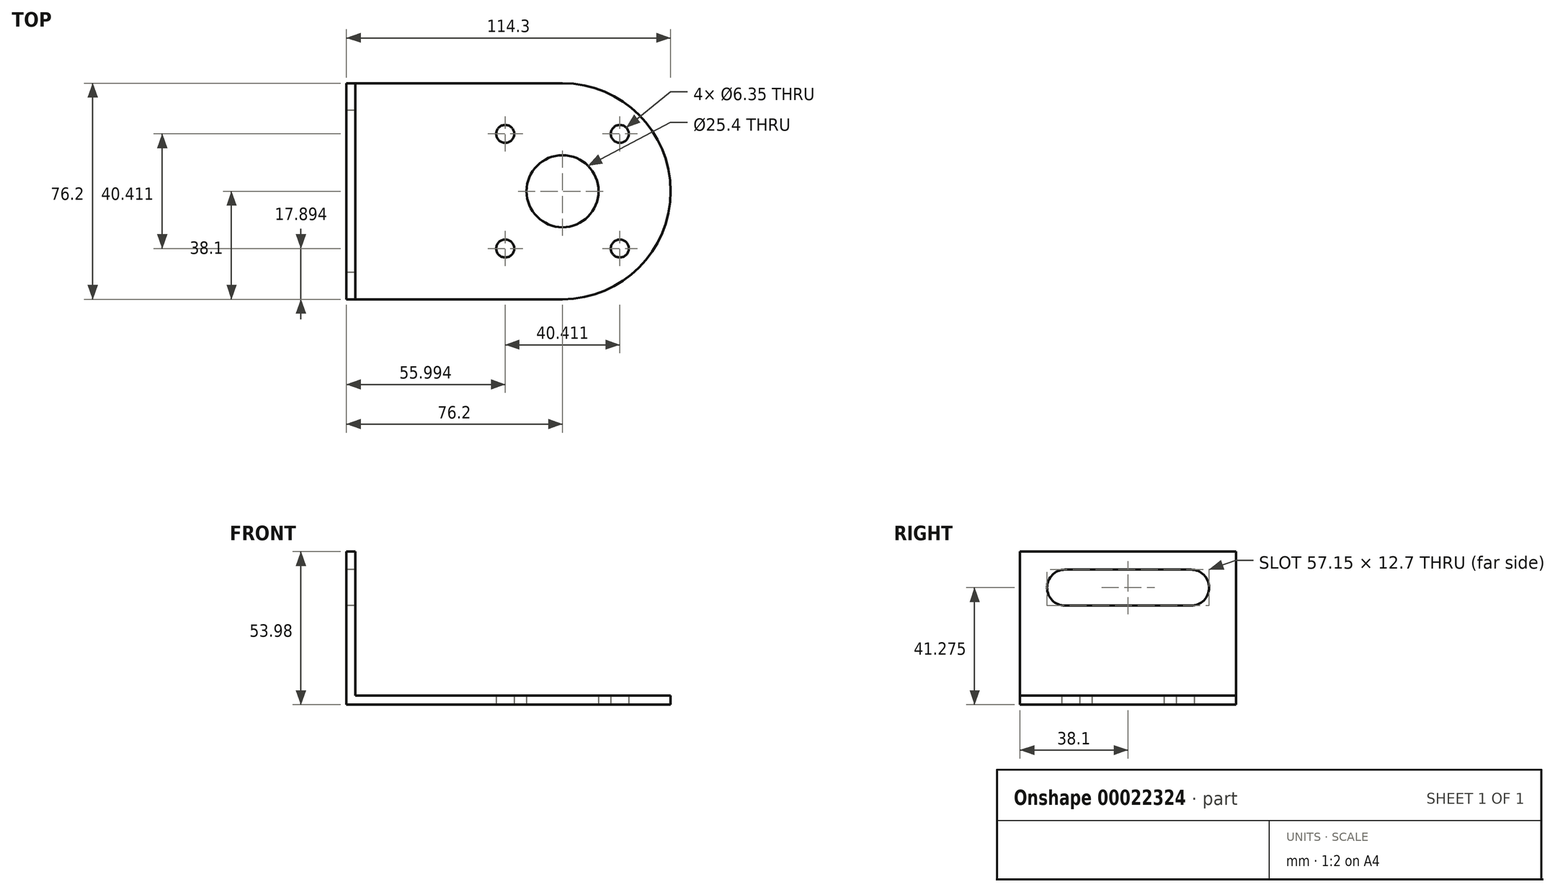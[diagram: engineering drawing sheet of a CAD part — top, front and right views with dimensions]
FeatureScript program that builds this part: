
annotation { "Feature Type Name" : "Feature", "Feature Type Description" : "" }
export const myFeature = defineFeature(function(context is Context, id is Id, definition is map)
    precondition{}
    {
        {
            var Q0;
            Q0=qCreatedBy(makeId("Top.planeOp"),FACE);
            var sketch = newSketch(context, id + "F0", { "sketchPlane" : qUnion([Q0])});
            skLineSegment(sketch, "E0.bottom", {"start": v(0, 76.2) * mm, "end": v(76.2, 76.2) * mm});
            skLineSegment(sketch, "E0.top", {"start": v(0, 0) * mm, "end": v(76.2, 0) * mm});
            skLineSegment(sketch, "E0.left", {"start": v(0, 76.2) * mm, "end": v(0, 0) * mm});
            skArc(sketch, "E1", {"start": v(76.2, 0) * mm, "mid": v(114.3, 38.1) * mm, "end": v(76.2, 76.2) * mm});
            skCircle(sketch, "E2", {"center": v(76.2, 38.1) * mm, "radius": 12.7 * mm});
            skCircle(sketch, "E3", {"center": v(76.2, 38.1) * mm, "radius": 28.58 * mm, "construction": true});
            skLineSegment(sketch, "E4", {"start": v(76.2, 38.1) * mm, "end": v(32.24, 38.1) * mm, "construction": true});
            skLineSegment(sketch, "E5", {"start": v(76.2, 38.1) * mm, "end": v(45.25, 69.05) * mm, "construction": true});
            skCircle(sketch, "E6", {"center": v(56, 58.3) * mm, "radius": 3.18 * mm});
            skCircle(sketch, "E7.1.0", {"center": v(56, 17.9) * mm, "radius": 3.18 * mm});
            skCircle(sketch, "E7.2.0", {"center": v(96.4, 17.9) * mm, "radius": 3.18 * mm});
            skCircle(sketch, "E7.3.0", {"center": v(96.4, 58.3) * mm, "radius": 3.18 * mm});
            skLineSegment(sketch, "E8", {"start": v(76.2, 38.1) * mm, "end": v(114.3, 38.1) * mm, "construction": true});
            skLineSegment(sketch, "E9", {"start": v(32.24, 38.1) * mm, "end": v(0, 38.1) * mm, "construction": true});
            skSolve(sketch);
        }
        {
            var Q0;
            Q0=qCreatedBy(makeId("Right.planeOp"),FACE);
            var sketch = newSketch(context, id + "F1", { "sketchPlane" : qUnion([Q0])});
            skLineSegment(sketch, "E10.bottom", {"start": v(0, 53.98) * mm, "end": v(76.2, 53.98) * mm});
            skLineSegment(sketch, "E10.top", {"start": v(0, 0) * mm, "end": v(76.2, 0) * mm});
            skLineSegment(sketch, "E10.left", {"start": v(0, 53.98) * mm, "end": v(0, 0) * mm});
            skLineSegment(sketch, "E10.right", {"start": v(76.2, 53.98) * mm, "end": v(76.2, 0) * mm});
            skLineSegment(sketch, "E11", {"start": v(0, 41.28) * mm, "end": v(76.2, 41.28) * mm, "construction": true});
            skArc(sketch, "E12", {"start": v(15.88, 47.63) * mm, "mid": v(9.53, 41.28) * mm, "end": v(15.88, 34.93) * mm});
            skArc(sketch, "E13", {"start": v(60.33, 34.93) * mm, "mid": v(66.67, 41.28) * mm, "end": v(60.33, 47.63) * mm});
            skLineSegment(sketch, "E14", {"start": v(15.88, 47.63) * mm, "end": v(60.33, 47.63) * mm});
            skLineSegment(sketch, "E15", {"start": v(60.33, 34.92) * mm, "end": v(15.88, 34.92) * mm});
            skSolve(sketch);
        }
        {
            var Q0;
            Q0 = qSketchRegion(id + "F1", true);
            extrude(context, id + "F2", {"entities" : qUnion([Q0]), "depth" : 3.17 * mm});
        }
        {
            var Q0;
            Q0 = qSketchRegion(id + "F0", true);
            extrude(context, id + "F3", {"entities" : qUnion([Q0]), "operationType" : NewBodyOperationType.ADD, "depth" : 3.17 * mm});
        }
    });
